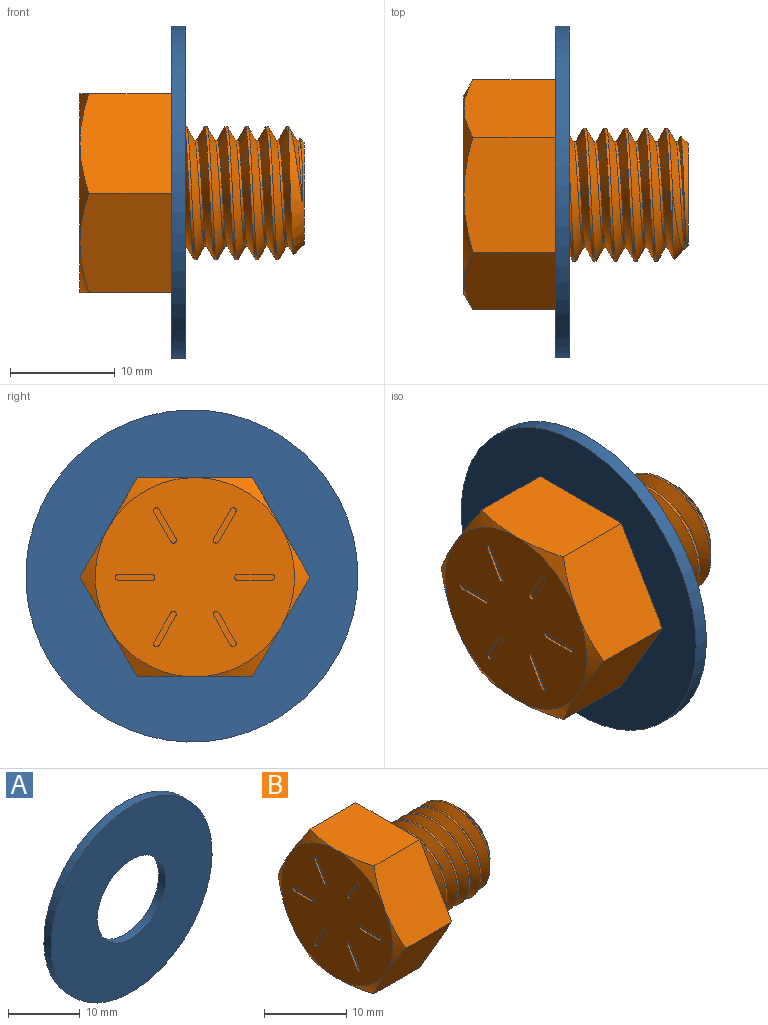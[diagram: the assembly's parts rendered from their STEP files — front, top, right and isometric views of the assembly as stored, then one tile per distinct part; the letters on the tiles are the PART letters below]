
ASSEMBLY  parts=2 mates=1
PART A: 4 faces, bbox 31.8x1.4x31.8 mm
  f0: cylinder r=15.88mm len=31.75mm, axis (0,-1,0), area 139.3mm2, adj f1,f2
  f1: plane 31.75x31.75mm, normal (0,1,0), area 648.9mm2, adj f0,f3
  f2: plane 31.75x31.75mm, normal (0,-1,0), area 648.9mm2, adj f0,f3
  f3: cylinder r=6.74mm len=13.49mm, axis (0,1,0), area 59.2mm2, adj f1,f2
PART B: 50 faces, bbox 22.7x22.9x22.9 mm
  f0: plane 11.91x9.64mm, normal (0,0,1), area 92.8mm2, adj f1,f5,f12,f13,f18
  f1: plane 10.43x9.64mm, normal (0,0.87,0.5), area 92.8mm2, adj f0,f2,f12,f17,f18
  f2: plane 10.43x9.64mm, normal (0,0.87,-0.5), area 92.8mm2, adj f1,f3,f12,f16,f17
  f3: plane 11.91x9.64mm, normal (0,0,-1), area 92.8mm2, adj f2,f4,f12,f15,f16
  f4: plane 10.43x9.64mm, normal (0,-0.87,-0.5), area 92.8mm2, adj f3,f5,f12,f14,f15
  f5: plane 10.43x9.64mm, normal (0,-0.87,0.5), area 92.8mm2, adj f0,f4,f12,f13,f14
  f6: cylinder r=6.35mm len=12.7mm, axis (1,0,0), area 51.4mm2, adj f7,f10,f11,f12
  f7: cone r=4.88mm half-angle=45deg, axis (-1,0,0), area 40mm2, adj f6,f8,f9,f10,f11
  f8: plane 9.77x9.77mm, normal (1,0,0), area 75mm2, adj f7
  f9: bspline ~13.14x10.69mm, area 49.9mm2, adj f7,f10,f11,f12
  f10: bspline ~13.43x13.35mm, area 319.4mm2, adj f6,f7,f9,f12
  f11: bspline ~13.82x13.35mm, area 307.8mm2, adj f6,f7,f9,f12
  f12: plane 22.75x19.81mm, normal (1,0,0), area 211mm2, adj f0,f1,f2,f3,f4,f5,f6,f9
  f13: cone r=9.53mm half-angle=60deg, axis (1,0,0), area 8.9mm2, adj f0,f5,f19
  f14: cone r=9.53mm half-angle=60deg, axis (1,0,0), area 8.9mm2, adj f4,f5,f19
  f15: cone r=9.53mm half-angle=60deg, axis (1,0,0), area 8.9mm2, adj f3,f4,f19
  f16: cone r=9.53mm half-angle=60deg, axis (1,0,0), area 8.9mm2, adj f2,f3,f19
  f17: cone r=9.53mm half-angle=60deg, axis (1,0,0), area 8.9mm2, adj f1,f2,f19
  f18: cone r=9.53mm half-angle=60deg, axis (1,0,0), area 8.9mm2, adj f0,f1,f19
  f19: plane 19.05x19.05mm, normal (-1,0,0), area 272.4mm2, adj f13,f14,f15,f16,f17,f18,f20,f21
  f20: cylinder r=0.29mm len=0.57mm, axis (-1,0,0), area 0.2mm2, adj f19,f21,f23,f24
  f21: plane 3.24x0.25mm, normal (0,0,-1), area 0.8mm2, adj f19,f20,f22,f24
  f22: cylinder r=0.29mm len=0.57mm, axis (-1,0,0), area 0.2mm2, adj f19,f21,f23,f24
  f23: plane 3.24x0.25mm, normal (0,0,1), area 0.8mm2, adj f19,f20,f22,f24
  f24: plane 3.81x0.57mm, normal (-1,0,0), area 2.1mm2, adj f20,f21,f22,f23
  f25: cylinder r=0.29mm len=0.53mm, axis (-1,0,0), area 0.2mm2, adj f19,f26,f28,f29
  f26: plane 2.8x1.62mm, normal (0,0.87,-0.5), area 0.8mm2, adj f19,f25,f27,f29
  f27: cylinder r=0.29mm len=0.53mm, axis (-1,0,0), area 0.2mm2, adj f19,f26,f28,f29
  f28: plane 2.8x1.62mm, normal (0,-0.87,0.5), area 0.8mm2, adj f19,f25,f27,f29
  f29: plane 3.38x2.19mm, normal (-1,0,0), area 2.1mm2, adj f25,f26,f27,f28
  f30: cylinder r=0.29mm len=0.53mm, axis (-1,0,0), area 0.2mm2, adj f19,f31,f33,f34
  f31: plane 2.8x1.62mm, normal (0,0.87,0.5), area 0.8mm2, adj f19,f30,f32,f34
  f32: cylinder r=0.29mm len=0.53mm, axis (-1,0,0), area 0.2mm2, adj f19,f31,f33,f34
  f33: plane 2.8x1.62mm, normal (0,-0.87,-0.5), area 0.8mm2, adj f19,f30,f32,f34
  f34: plane 3.38x2.19mm, normal (-1,0,0), area 2.1mm2, adj f30,f31,f32,f33
  f35: cylinder r=0.29mm len=0.57mm, axis (-1,0,0), area 0.2mm2, adj f19,f36,f38,f39
  f36: plane 3.24x0.25mm, normal (0,0,1), area 0.8mm2, adj f19,f35,f37,f39
  f37: cylinder r=0.29mm len=0.57mm, axis (-1,0,0), area 0.2mm2, adj f19,f36,f38,f39
  f38: plane 3.24x0.25mm, normal (0,0,-1), area 0.8mm2, adj f19,f35,f37,f39
  f39: plane 3.81x0.57mm, normal (-1,0,0), area 2.1mm2, adj f35,f36,f37,f38
  f40: cylinder r=0.29mm len=0.53mm, axis (-1,0,0), area 0.2mm2, adj f19,f41,f43,f44
  f41: plane 2.8x1.62mm, normal (0,-0.87,0.5), area 0.8mm2, adj f19,f40,f42,f44
  f42: cylinder r=0.29mm len=0.53mm, axis (-1,0,0), area 0.2mm2, adj f19,f41,f43,f44
  f43: plane 2.8x1.62mm, normal (0,0.87,-0.5), area 0.8mm2, adj f19,f40,f42,f44
  f44: plane 3.38x2.19mm, normal (-1,0,0), area 2.1mm2, adj f40,f41,f42,f43
  f45: cylinder r=0.29mm len=0.53mm, axis (-1,0,0), area 0.2mm2, adj f19,f46,f48,f49
  f46: plane 2.8x1.62mm, normal (0,-0.87,-0.5), area 0.8mm2, adj f19,f45,f47,f49
  f47: cylinder r=0.29mm len=0.53mm, axis (-1,0,0), area 0.2mm2, adj f19,f46,f48,f49
  f48: plane 2.8x1.62mm, normal (0,0.87,0.5), area 0.8mm2, adj f19,f45,f47,f49
  f49: plane 3.38x2.19mm, normal (-1,0,0), area 2.1mm2, adj f45,f46,f47,f48
PLACE A rot(axis=(0.58,0.58,-0.58),120deg) t=(-1.98,0.29,0.12)mm
PLACE B at identity
MATE fastened A.f0 <-> B.f12  axis (-1,0,0) through (-1.98,0.29,0.12)mm
